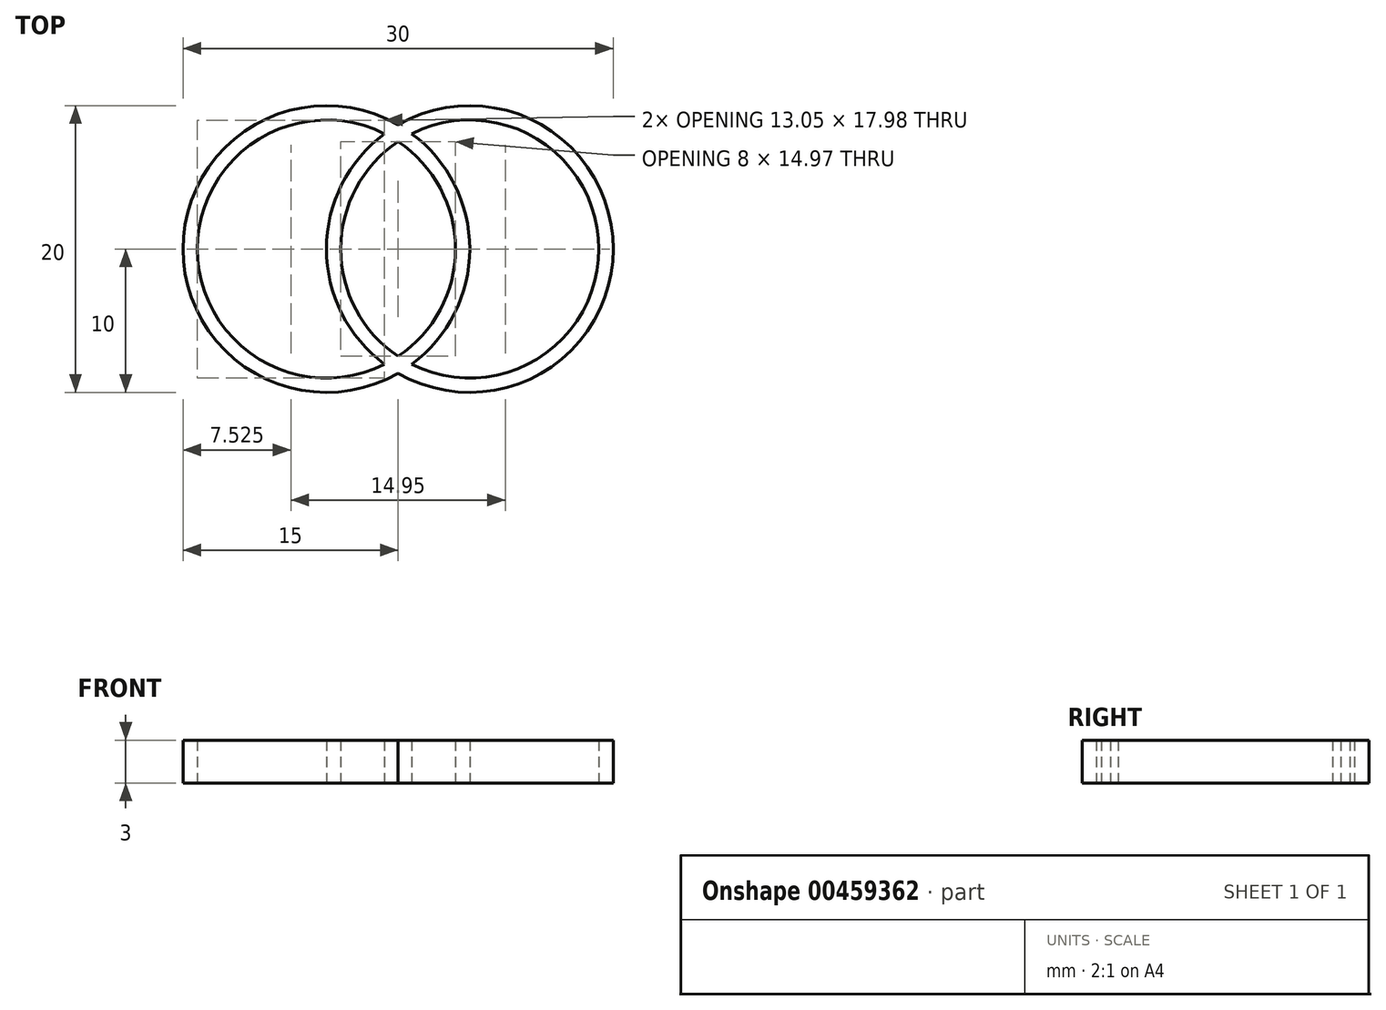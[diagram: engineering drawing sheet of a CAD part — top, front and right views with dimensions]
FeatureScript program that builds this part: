
annotation { "Feature Type Name" : "Feature", "Feature Type Description" : "" }
export const myFeature = defineFeature(function(context is Context, id is Id, definition is map)
    precondition{}
    {
        {
            var Q0;
            Q0=qCreatedBy(makeId("Top.planeOp"),FACE);
            var sketch = newSketch(context, id + "F0", { "sketchPlane" : qUnion([Q0])});
            skLineSegment(sketch, "E0", {"start": v(0, 0) * mm, "end": v(-5, 0) * mm});
            skLineSegment(sketch, "E1", {"start": v(0, 0) * mm, "end": v(5, 0) * mm});
            skLineSegment(sketch, "E2", {"start": v(0, 0) * mm, "end": v(0, 7.48) * mm});
            skArc(sketch, "E3", {"start": v(0, 8.66) * mm, "mid": v(-15, 0) * mm, "end": v(0, -8.66) * mm});
            skArc(sketch, "E4", {"start": v(-0.95, 8.04) * mm, "mid": v(-5, 0) * mm, "end": v(-0.95, -8.04) * mm});
            skLineSegment(sketch, "E5", {"start": v(0, 7.48) * mm, "end": v(0, -8.66) * mm});
            skArc(sketch, "E6", {"start": v(-0.95, 8.04) * mm, "mid": v(-14, 0) * mm, "end": v(-0.95, -8.04) * mm});
            skArc(sketch, "E7", {"start": v(0, 7.48) * mm, "mid": v(-4, 0) * mm, "end": v(0, -7.48) * mm});
            skLineSegment(sketch, "E8.trimOffspring", {"start": v(0, 8.66) * mm, "end": v(0, 50.86) * mm});
            skArc(sketch, "E9.trimOffspring", {"start": v(0, -8.66) * mm, "mid": v(15, 0) * mm, "end": v(0, 8.66) * mm});
            skArc(sketch, "E10.trimOffspring", {"start": v(0.95, -8.04) * mm, "mid": v(14, 0) * mm, "end": v(0.95, 8.04) * mm});
            skArc(sketch, "E11.trimOffspring", {"start": v(0, -7.48) * mm, "mid": v(4, 0) * mm, "end": v(0, 7.48) * mm});
            skArc(sketch, "E12.trimOffspring", {"start": v(0.95, -8.04) * mm, "mid": v(5, 0) * mm, "end": v(0.95, 8.04) * mm});
            skSolve(sketch);
        }
        {
            var Q0;
            Q0=makeQuery(id+"F0.imprint","IMPRINT",FACE,{"disambiguationData":[TD([[makeQuery(id+"F0.imprint","IMPRINT",EDGE,{"derivedFrom":sQuery(id+"F0.wireOp",EDGE,"E3")}),1.0]])]});
            extrude(context, id + "F1", {"entities" : qUnion([Q0]), "depth" : 3 * mm});
        }
    });
